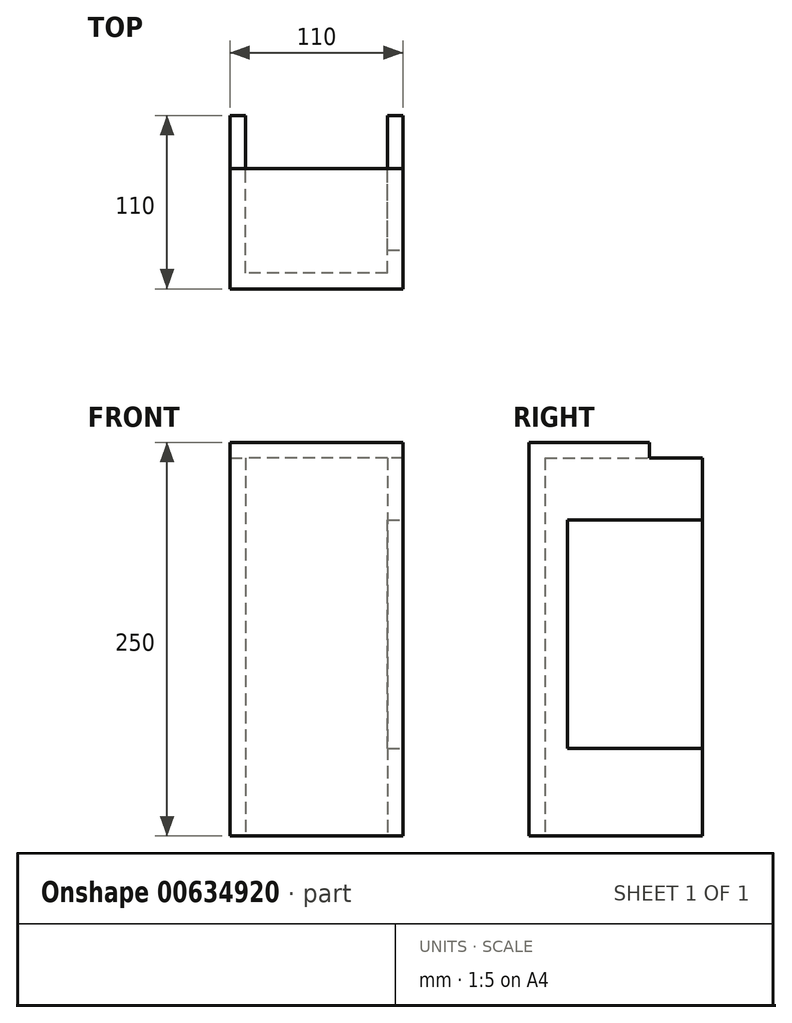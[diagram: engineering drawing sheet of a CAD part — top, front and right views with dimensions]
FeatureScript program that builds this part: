
annotation { "Feature Type Name" : "Feature", "Feature Type Description" : "" }
export const myFeature = defineFeature(function(context is Context, id is Id, definition is map)
    precondition{}
    {
        {
            var Q0;
            Q0=qCreatedBy(makeId("Top.planeOp"),FACE);
            var sketch = newSketch(context, id + "F0", { "sketchPlane" : qUnion([Q0])});
            skLineSegment(sketch, "E0.bottom", {"start": v(0, 0) * mm, "end": v(-110, 0) * mm});
            skLineSegment(sketch, "E0.top", {"start": v(-10, 10) * mm, "end": v(-100, 10) * mm});
            skLineSegment(sketch, "E0.left", {"start": v(0, 0) * mm, "end": v(0, 10) * mm});
            skLineSegment(sketch, "E0.right", {"start": v(-110, 0) * mm, "end": v(-110, 10) * mm});
            skLineSegment(sketch, "E1.top", {"start": v(-110, 110) * mm, "end": v(-100, 110) * mm});
            skLineSegment(sketch, "E1.left", {"start": v(-110, 10) * mm, "end": v(-110, 110) * mm});
            skLineSegment(sketch, "E1.right", {"start": v(-100, 10) * mm, "end": v(-100, 110) * mm});
            skLineSegment(sketch, "E2.top", {"start": v(0, 110) * mm, "end": v(-10, 110) * mm});
            skLineSegment(sketch, "E2.left", {"start": v(0, 10) * mm, "end": v(0, 110) * mm});
            skLineSegment(sketch, "E2.right", {"start": v(-10, 10) * mm, "end": v(-10, 110) * mm});
            skSolve(sketch);
        }
        {
            var Q0;
            Q0 = qSketchRegion(id + "F0", true);
            extrude(context, id + "F1", {"entities" : qUnion([Q0]), "depth" : 240 * mm, "offsetDistance" : 25 * mm});
        }
        {
            var Q0;
            Q0=makeQuery(id+"F1.opExtrude","SWEPT_FACE",FACE,{"disambiguationData":[OSD([sQuery(id+"F0.wireOp",EDGE,"E0.left"),sQuery(id+"F0.wireOp",EDGE,"E2.left")])]});
            var sketch = newSketch(context, id + "F2", { "sketchPlane" : qUnion([Q0])});
            skLineSegment(sketch, "E3.bottom", {"start": v(110, 200.6) * mm, "end": v(24.46, 200.6) * mm});
            skLineSegment(sketch, "E3.top", {"start": v(110, 55.6) * mm, "end": v(24.46, 55.6) * mm});
            skLineSegment(sketch, "E3.left", {"start": v(110, 200.6) * mm, "end": v(110, 55.6) * mm});
            skLineSegment(sketch, "E3.right", {"start": v(24.46, 200.6) * mm, "end": v(24.46, 55.6) * mm});
            skSolve(sketch);
        }
        {
            var Q0;
            Q0 = qSketchRegion(id + "F2", true);
            extrude(context, id + "F3", {"entities" : qUnion([Q0]), "operationType" : NewBodyOperationType.REMOVE, "oppositeDirection" : true, "depth" : 25 * mm, "offsetDistance" : 25 * mm});
        }
        {
            var Q0;
            Q0=makeQuery(id+"F1.opExtrude","CAP_FACE",FACE,{"disambiguationData":[OSD([sQuery(id+"F0.wireOp",EDGE,"E0.bottom"),sQuery(id+"F0.wireOp",EDGE,"E0.top"),sQuery(id+"F0.wireOp",EDGE,"E0.left"),sQuery(id+"F0.wireOp",EDGE,"E0.right"),sQuery(id+"F0.wireOp",EDGE,"E1.top"),sQuery(id+"F0.wireOp",EDGE,"E1.left"),sQuery(id+"F0.wireOp",EDGE,"E1.right"),sQuery(id+"F0.wireOp",EDGE,"E2.top"),sQuery(id+"F0.wireOp",EDGE,"E2.left"),sQuery(id+"F0.wireOp",EDGE,"E2.right")])],"isStart":false});
            var sketch = newSketch(context, id + "F4", { "sketchPlane" : qUnion([Q0])});
            skLineSegment(sketch, "E4.bottom", {"start": v(0, 76.37) * mm, "end": v(-110, 76.37) * mm});
            skLineSegment(sketch, "E4.top", {"start": v(0, 0) * mm, "end": v(-110, 0) * mm});
            skLineSegment(sketch, "E4.left", {"start": v(0, 76.37) * mm, "end": v(0, 0) * mm});
            skLineSegment(sketch, "E4.right", {"start": v(-110, 76.37) * mm, "end": v(-110, 0) * mm});
            skSolve(sketch);
        }
        {
            var Q0;
            Q0 = qSketchRegion(id + "F4", true);
            extrude(context, id + "F5", {"entities" : qUnion([Q0]), "operationType" : NewBodyOperationType.ADD, "depth" : 10 * mm, "offsetDistance" : 25 * mm});
        }
    });
